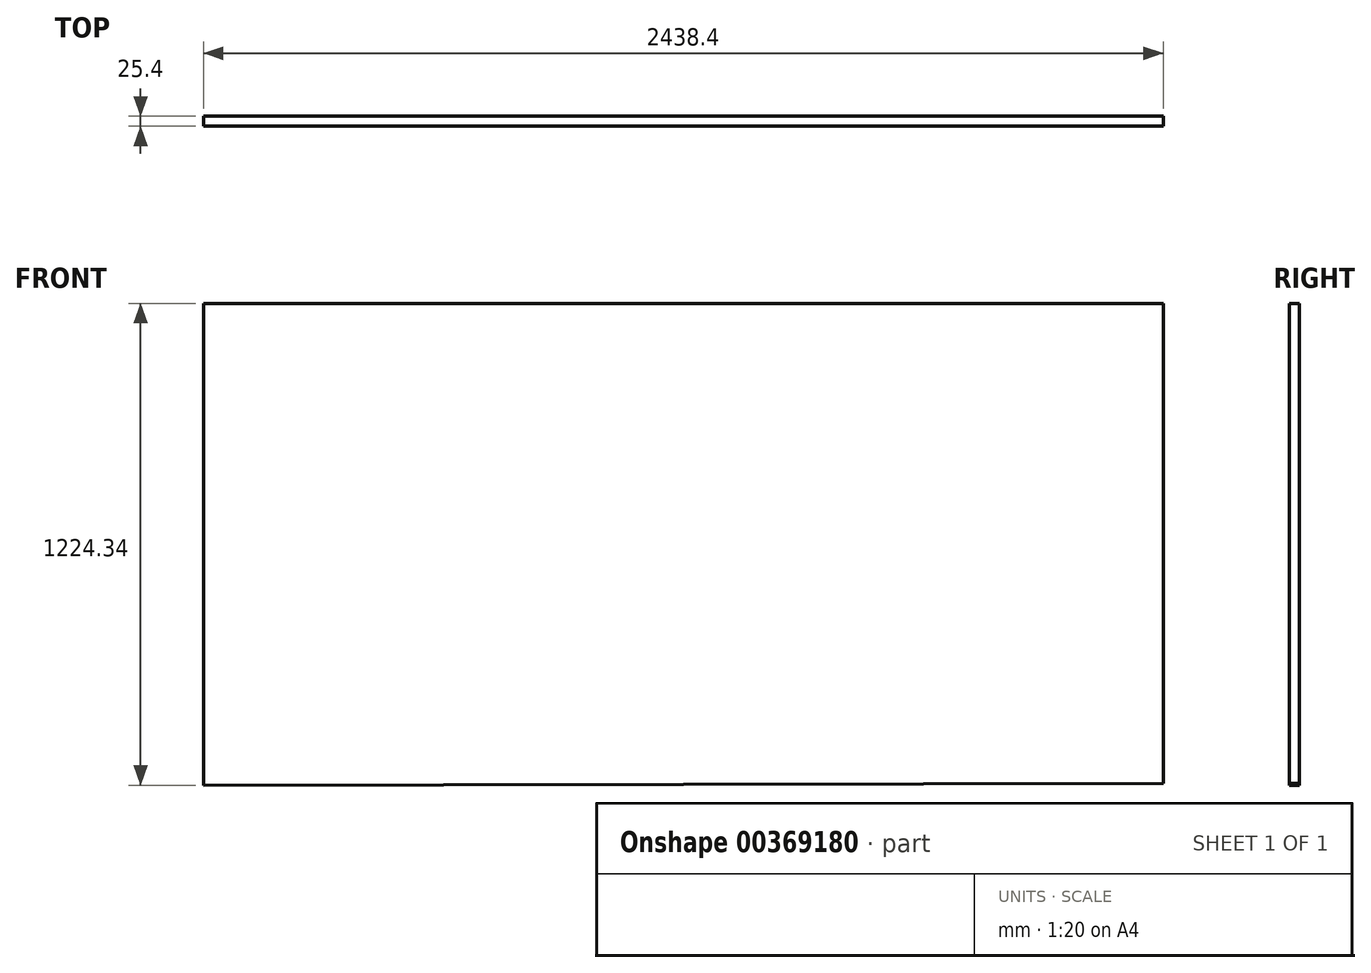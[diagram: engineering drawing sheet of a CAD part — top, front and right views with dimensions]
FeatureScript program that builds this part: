
annotation { "Feature Type Name" : "Feature", "Feature Type Description" : "" }
export const myFeature = defineFeature(function(context is Context, id is Id, definition is map)
    precondition{}
    {
        {
            var Q0;
            Q0=qCreatedBy(makeId("Front.planeOp"),FACE);
            var sketch = newSketch(context, id + "F0", { "sketchPlane" : qUnion([Q0])});
            skLineSegment(sketch, "E0", {"start": v(-918.11, 743.03) * mm, "end": v(-918.11, -481.3) * mm});
            skLineSegment(sketch, "E1", {"start": v(-918.11, 743.03) * mm, "end": v(1520.29, 743.03) * mm});
            skLineSegment(sketch, "E2", {"start": v(1520.29, 743.03) * mm, "end": v(1520.29, -476.17) * mm});
            skLineSegment(sketch, "E3", {"start": v(1520.29, -476.17) * mm, "end": v(-918.11, -481.3) * mm});
            skSolve(sketch);
        }
        {
            var Q0;
            Q0=makeQuery(id+"F0.imprint","IMPRINT",FACE,{"disambiguationData":[TD([[makeQuery(id+"F0.imprint","IMPRINT",EDGE,{"derivedFrom":sQuery(id+"F0.wireOp",EDGE,"E0")}),1.0]])]});
            extrude(context, id + "F1", {"entities" : qUnion([Q0]), "depth" : 25.4 * mm});
        }
    });
